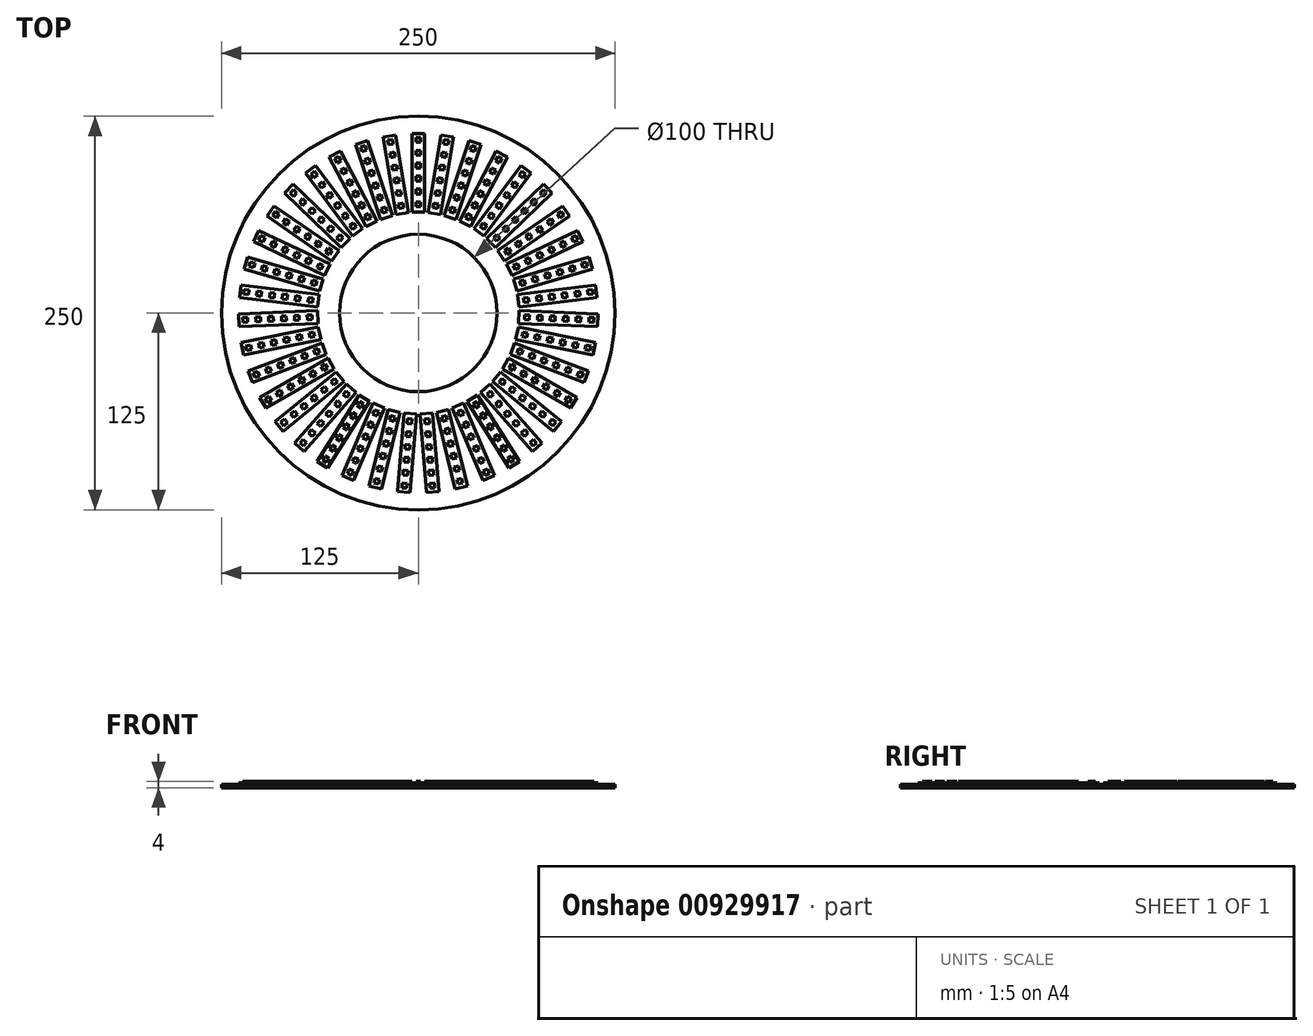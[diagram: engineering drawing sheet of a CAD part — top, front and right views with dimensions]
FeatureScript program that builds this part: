
annotation { "Feature Type Name" : "Feature", "Feature Type Description" : "" }
export const myFeature = defineFeature(function(context is Context, id is Id, definition is map)
    precondition{}
    {
        {
            var Q0;
            Q0=qCreatedBy(makeId("Top.planeOp"),FACE);
            var sketch = newSketch(context, id + "F0", { "sketchPlane" : qUnion([Q0])});
            skCircle(sketch, "E0", {"center": v(0, 0) * mm, "radius": 50 * mm});
            skCircle(sketch, "E1", {"center": v(0, 0) * mm, "radius": 125 * mm});
            skSolve(sketch);
        }
        {
            var Q0;
            Q0 = qSketchRegion(id + "F0", true);
            extrude(context, id + "F1", {"entities" : qUnion([Q0]), "depth" : 2 * mm, "offsetDistance" : 25 * mm});
        }
        {
            var Q0;
            Q0=makeQuery(id+"F1.opExtrude","CAP_FACE",FACE,{"disambiguationData":[OSD([sQuery(id+"F0.wireOp",EDGE,"E0"),sQuery(id+"F0.wireOp",EDGE,"E1")])],"isStart":false});
            var sketch = newSketch(context, id + "F2", { "sketchPlane" : qUnion([Q0])});
            skLineSegment(sketch, "E2.bottom", {"start": v(-4, 64) * mm, "end": v(4, 64) * mm});
            skLineSegment(sketch, "E2.top", {"start": v(-4, 114) * mm, "end": v(4, 114) * mm});
            skLineSegment(sketch, "E2.left", {"start": v(-4, 64) * mm, "end": v(-4, 114) * mm});
            skLineSegment(sketch, "E2.right", {"start": v(4, 64) * mm, "end": v(4, 114) * mm});
            skLineSegment(sketch, "E3", {"start": v(0, 0) * mm, "end": v(0, 125) * mm, "construction": true});
            skSolve(sketch);
        }
        {
            var Q0;
            Q0=makeQuery(id+"F2.imprint","IMPRINT",FACE,{"disambiguationData":[TD([[makeQuery(id+"F2.imprint","IMPRINT",EDGE,{"derivedFrom":sQuery(id+"F2.wireOp",EDGE,"E2.bottom")}),1.0]])]});
            extrude(context, id + "F3", {"entities" : qUnion([Q0]), "operationType" : NewBodyOperationType.ADD, "depth" : 1 * mm, "offsetDistance" : 25 * mm});
        }
        {
            var Q0;
            Q0=makeQuery(id+"F3.opExtrude","CAP_FACE",FACE,{"disambiguationData":[OSD([sQuery(id+"F2.wireOp",EDGE,"E2.bottom"),sQuery(id+"F2.wireOp",EDGE,"E2.top"),sQuery(id+"F2.wireOp",EDGE,"E2.left"),sQuery(id+"F2.wireOp",EDGE,"E2.right")])],"isStart":false});
            var sketch = newSketch(context, id + "F4", { "sketchPlane" : qUnion([Q0])});
            skLineSegment(sketch, "E4.bottom", {"start": v(-1.5, 108.5) * mm, "end": v(1.5, 108.5) * mm});
            skLineSegment(sketch, "E4.top", {"start": v(-1.5, 111.5) * mm, "end": v(1.5, 111.5) * mm});
            skLineSegment(sketch, "E4.left", {"start": v(-1.5, 108.5) * mm, "end": v(-1.5, 111.5) * mm});
            skLineSegment(sketch, "E4.right", {"start": v(1.5, 108.5) * mm, "end": v(1.5, 111.5) * mm});
            skLineSegment(sketch, "E5", {"start": v(-1.5, 114) * mm, "end": v(-1.5, 64) * mm, "construction": true});
            skLineSegment(sketch, "E6.1.0.0", {"start": v(-1.5, 100.3) * mm, "end": v(1.5, 100.3) * mm});
            skLineSegment(sketch, "E6.1.0.1", {"start": v(1.5, 100.3) * mm, "end": v(1.5, 103.3) * mm});
            skLineSegment(sketch, "E6.1.0.2", {"start": v(-1.5, 103.3) * mm, "end": v(1.5, 103.3) * mm});
            skLineSegment(sketch, "E6.1.0.3", {"start": v(-1.5, 100.3) * mm, "end": v(-1.5, 103.3) * mm});
            skLineSegment(sketch, "E6.2.0.0", {"start": v(-1.5, 92.1) * mm, "end": v(1.5, 92.1) * mm});
            skLineSegment(sketch, "E6.2.0.1", {"start": v(1.5, 92.1) * mm, "end": v(1.5, 95.1) * mm});
            skLineSegment(sketch, "E6.2.0.2", {"start": v(-1.5, 95.1) * mm, "end": v(1.5, 95.1) * mm});
            skLineSegment(sketch, "E6.2.0.3", {"start": v(-1.5, 92.1) * mm, "end": v(-1.5, 95.1) * mm});
            skLineSegment(sketch, "E6.direction1", {"start": v(-1.5, 108.5) * mm, "end": v(-1.5, 100.3) * mm, "construction": true});
            skLineSegment(sketch, "E7.0.3.0", {"start": v(-1.5, 83.9) * mm, "end": v(1.5, 83.9) * mm});
            skLineSegment(sketch, "E7.3.3.0", {"start": v(1.5, 83.9) * mm, "end": v(1.5, 86.9) * mm});
            skLineSegment(sketch, "E7.6.3.0", {"start": v(-1.5, 86.9) * mm, "end": v(1.5, 86.9) * mm});
            skLineSegment(sketch, "E7.9.3.0", {"start": v(-1.5, 83.9) * mm, "end": v(-1.5, 86.9) * mm});
            skLineSegment(sketch, "E7.0.4.0", {"start": v(-1.5, 75.7) * mm, "end": v(1.5, 75.7) * mm});
            skLineSegment(sketch, "E7.3.4.0", {"start": v(1.5, 75.7) * mm, "end": v(1.5, 78.7) * mm});
            skLineSegment(sketch, "E7.6.4.0", {"start": v(-1.5, 78.7) * mm, "end": v(1.5, 78.7) * mm});
            skLineSegment(sketch, "E7.9.4.0", {"start": v(-1.5, 75.7) * mm, "end": v(-1.5, 78.7) * mm});
            skLineSegment(sketch, "E7.0.5.0", {"start": v(-1.5, 67.5) * mm, "end": v(1.5, 67.5) * mm});
            skLineSegment(sketch, "E7.3.5.0", {"start": v(1.5, 67.5) * mm, "end": v(1.5, 70.5) * mm});
            skLineSegment(sketch, "E7.6.5.0", {"start": v(-1.5, 70.5) * mm, "end": v(1.5, 70.5) * mm});
            skLineSegment(sketch, "E7.9.5.0", {"start": v(-1.5, 67.5) * mm, "end": v(-1.5, 70.5) * mm});
            skSolve(sketch);
        }
        {
            var Q0;
            Q0 = qSketchRegion(id + "F4", true);
            extrude(context, id + "F5", {"entities" : qUnion([Q0]), "operationType" : NewBodyOperationType.ADD, "depth" : 1 * mm, "offsetDistance" : 25 * mm});
        }
        {
            var Q0;
            Q0=qCreatedBy(makeId("Right.planeOp"),FACE);
            var sketch = newSketch(context, id + "F6", { "sketchPlane" : qUnion([Q0])});
            skLineSegment(sketch, "E8", {"start": v(0, 0) * mm, "end": v(0, 34.94) * mm, "construction": true});
            skSolve(sketch);
        }
        {
            var Q0;
            Q0=makeQuery(id+"F1.opExtrude","SWEPT_BODY",BODY,{"disambiguationData":[OSD([sQuery(id+"F0.wireOp",EDGE,"E0"),sQuery(id+"F0.wireOp",EDGE,"E1")])]});
            var Q1;
            Q1=sQuery(id+"F6.wireOp",EDGE,"E8");
            circularPattern(context, id + "F7", {"operationType" : NewBodyOperationType.ADD, "entities" : qUnion([Q0]), "axis" : qUnion([Q1]), "angle" : 360 * degree, "instanceCount" : 39, "equalSpace" : true});
        }
    });
